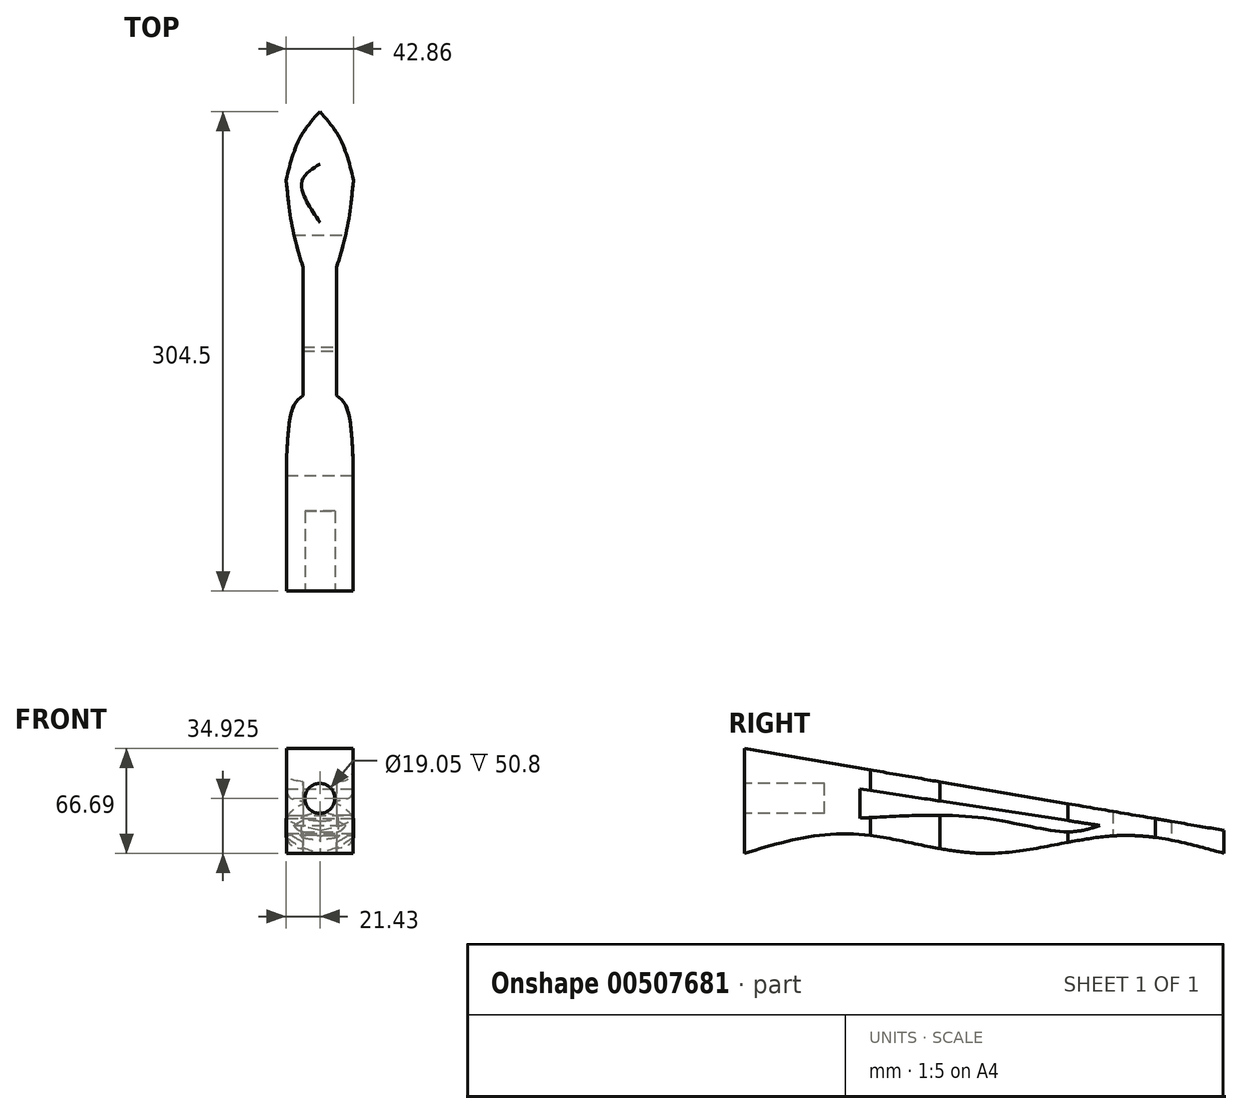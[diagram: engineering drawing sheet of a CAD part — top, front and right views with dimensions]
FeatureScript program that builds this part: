
annotation { "Feature Type Name" : "Feature", "Feature Type Description" : "" }
export const myFeature = defineFeature(function(context is Context, id is Id, definition is map)
    precondition{}
    {
        {
            var Q0;
            Q0=qCreatedBy(makeId("Right.planeOp"),FACE);
            var sketch = newSketch(context, id + "F0", { "sketchPlane" : qUnion([Q0])});
            skLineSegment(sketch, "E0", {"start": v(-152.4, 0) * mm, "end": v(152.4, 0) * mm});
            skLineSegment(sketch, "E1", {"start": v(-152.4, 0) * mm, "end": v(-152.4, 69.85) * mm});
            skLineSegment(sketch, "E2", {"start": v(152.4, 0) * mm, "end": v(152.4, 19.05) * mm});
            skLineSegment(sketch, "E3", {"start": v(152.4, 19.05) * mm, "end": v(-152.4, 69.85) * mm});
            skPoint(sketch, "E4.endSnap0", {"position": v(-152.4, 34.93) * mm});
            skLineSegment(sketch, "E5.0", {"start": v(-95.25, 50.8) * mm, "end": v(-152.4, 50.8) * mm, "construction": true});
            skLineSegment(sketch, "E5.1", {"start": v(-95.25, 50.8) * mm, "end": v(-95.25, 19.05) * mm, "construction": true});
            skLineSegment(sketch, "E5.2", {"start": v(-95.25, 19.05) * mm, "end": v(-152.4, 19.05) * mm, "construction": true});
            skSolve(sketch);
        }
        {
            var Q0;
            Q0=makeQuery(id+"F0.imprint","IMPRINT",FACE,{"disambiguationData":[TD([[makeQuery(id+"F0.imprint","IMPRINT",EDGE,{"derivedFrom":sQuery(id+"F0.wireOp",EDGE,"E0")}),1.0]])]});
            extrude(context, id + "F1", {"entities" : qUnion([Q0]), "depth" : 42.86 * mm, "symmetric" : true});
        }
        {
            var Q0;
            Q0=makeQuery(id+"F1.opExtrude","SWEPT_FACE",FACE,{"disambiguationData":[OSD([sQuery(id+"F0.wireOp",EDGE,"E1")])]});
            var sketch = newSketch(context, id + "F2", { "sketchPlane" : qUnion([Q0])});
            skLineSegment(sketch, "E6", {"start": v(21.43, 34.93) * mm, "end": v(0, 34.93) * mm, "construction": true});
            skCircle(sketch, "E7", {"center": v(0, 34.93) * mm, "radius": 9.53 * mm});
            skSolve(sketch);
        }
        {
            var Q0;
            Q0=makeQuery(id+"F2.imprint","IMPRINT",FACE,{"disambiguationData":[TD([[makeQuery(id+"F2.imprint","IMPRINT",EDGE,{"derivedFrom":sQuery(id+"F2.wireOp",EDGE,"E7")}),1.0]])]});
            var Q1;
            Q1=sQuery(id+"F2.wireOp",EDGE,"E7");
            extrude(context, id + "F3", {"entities" : qUnion([Q0]), "operationType" : NewBodyOperationType.REMOVE, "surfaceEntities" : qUnion([Q1]), "oppositeDirection" : true, "depth" : 50.8 * mm});
        }
        {
            var Q0;
            Q0=makeQuery(id+"F1.opExtrude","CAP_FACE",FACE,{"disambiguationData":[OSD([sQuery(id+"F0.wireOp",EDGE,"E0"),sQuery(id+"F0.wireOp",EDGE,"E1"),sQuery(id+"F0.wireOp",EDGE,"E2"),sQuery(id+"F0.wireOp",EDGE,"E3")])],"isStart":false});
            var sketch = newSketch(context, id + "F4", { "sketchPlane" : qUnion([Q0])});
            skLineSegment(sketch, "E8", {"start": v(-152.4, 34.93) * mm, "end": v(-152.4, 44.45) * mm, "construction": true});
            skLineSegment(sketch, "E9.0", {"start": v(-95.25, 19.05) * mm, "end": v(-152.4, 19.05) * mm, "construction": true});
            skLineSegment(sketch, "E9.1", {"start": v(-95.25, 50.8) * mm, "end": v(-95.25, 19.05) * mm, "construction": true});
            skLineSegment(sketch, "E9.2", {"start": v(-152.4, 50.8) * mm, "end": v(-95.25, 50.8) * mm, "construction": true});
            skLineSegment(sketch, "E10", {"start": v(57.15, 0) * mm, "end": v(57.15, 34.93) * mm, "construction": true});
            skLineSegment(sketch, "E11", {"start": v(-152.4, 44.45) * mm, "end": v(-101.6, 44.45) * mm, "construction": true});
            skLineSegment(sketch, "E12", {"start": v(-101.6, 44.45) * mm, "end": v(-101.6, 25.4) * mm, "construction": true});
            skLineSegment(sketch, "E13", {"start": v(-101.6, 25.4) * mm, "end": v(-152.4, 25.4) * mm, "construction": true});
            skSolve(sketch);
        }
        {
            var Q0;
            Q0=makeQuery(id+"F1.opExtrude","SWEPT_FACE",FACE,{"disambiguationData":[OSD([sQuery(id+"F0.wireOp",EDGE,"E0")])]});
            var sketch = newSketch(context, id + "F5", { "sketchPlane" : qUnion([Q0])});
            skLineSegment(sketch, "E14", {"start": v(0, 152.4) * mm, "end": v(0, -152.4) * mm, "construction": true});
            skLineSegment(sketch, "E15", {"start": v(21.43, -57.15) * mm, "end": v(-21.43, -57.15) * mm, "construction": true});
            skLineSegment(sketch, "E16", {"start": v(15.88, 152.4) * mm, "end": v(15.88, 95.25) * mm, "construction": true});
            skLineSegment(sketch, "E17", {"start": v(15.88, 95.25) * mm, "end": v(-15.87, 95.25) * mm, "construction": true});
            skLineSegment(sketch, "E18", {"start": v(-15.87, 95.25) * mm, "end": v(-15.87, 152.4) * mm, "construction": true});
            skLineSegment(sketch, "E19", {"start": v(0, 152.4) * mm, "end": v(-9.53, 152.4) * mm, "construction": true});
            skLineSegment(sketch, "E20", {"start": v(-9.53, 152.4) * mm, "end": v(-9.53, 101.6) * mm, "construction": true});
            skLineSegment(sketch, "E21", {"start": v(-9.52, 101.6) * mm, "end": v(9.53, 101.6) * mm, "construction": true});
            skLineSegment(sketch, "E22", {"start": v(9.53, 101.6) * mm, "end": v(9.53, 152.4) * mm, "construction": true});
            skSolve(sketch);
        }
        {
            var Q0;
            Q0=makeQuery(id+"F4.imprint","IMPRINT",FACE,{"disambiguationData":[TD([[makeQuery(id+"F4.imprint","IMPRINT",EDGE,{"derivedFrom":makeQuery(id+"F1.opExtrude","CAP_EDGE",EDGE,{"disambiguationData":[OSD([sQuery(id+"F0.wireOp",EDGE,"E0")])],"isStart":false})}),1.0]])]});
            var sketch = newSketch(context, id + "F6", { "sketchPlane" : qUnion([Q0])});
            skFitSpline(sketch, "E23", {"points": [v(-152.45, 0) * mm, v(-83.19, 12.39) * mm, v(0, 0) * mm, v(84.2, 11.28) * mm, v(152.36, 0) * mm], "startDerivative": vector(283.15, 85.12) * mm, "endDerivative": vector(279.7, -78.66) * mm});
            skLineSegment(sketch, "E24", {"start": v(152.36, 0) * mm, "end": v(152.36, 14.6) * mm});
            skLineSegment(sketch, "E25", {"start": v(152.36, 14.6) * mm, "end": v(-152.9, 66.78) * mm});
            skLineSegment(sketch, "E26", {"start": v(-152.9, 66.78) * mm, "end": v(-152.45, 0) * mm});
            skLineSegment(sketch, "E27", {"start": v(-78.97, 41.03) * mm, "end": v(-78.97, 22.38) * mm});
            skFitSpline(sketch, "E28", {"points": [v(-78.97, 22.38) * mm, v(0, 22.38) * mm, v(52.02, 13.72) * mm, v(73.55, 17.72) * mm], "startDerivative": vector(190.9, 11.16) * mm, "endDerivative": vector(86.31, 27.92) * mm});
            skLineSegment(sketch, "E29", {"start": v(-78.97, 41.03) * mm, "end": v(73.55, 17.72) * mm});
            skSolve(sketch);
        }
        {
            var Q0;
            Q0 = qSketchRegion(id + "F6", true);
            extrude(context, id + "F7", {"entities" : qUnion([Q0]), "operationType" : NewBodyOperationType.INTERSECT, "endBound" : BoundingType.THROUGH_ALL, "oppositeDirection" : true, "depth" : 25.4 * mm});
        }
        {
            var Q0;
            Q0=qCreatedBy(makeId("Top.planeOp"),FACE);
            var sketch = newSketch(context, id + "F8", { "sketchPlane" : qUnion([Q0])});
            skLineSegment(sketch, "E30", {"start": v(21.25, -152.7) * mm, "end": v(21.25, -72.27) * mm});
            skFitSpline(sketch, "E31", {"points": [v(21.25, -72.27) * mm, v(16.78, -35.22) * mm, v(10.67, -28.28) * mm], "startDerivative": vector(-2.79, 67.04) * mm, "endDerivative": vector(-20.34, 15.12) * mm});
            skLineSegment(sketch, "E32", {"start": v(10.67, -28.28) * mm, "end": v(10.67, 53.23) * mm});
            skFitSpline(sketch, "E33", {"points": [v(10.67, 53.23) * mm, v(17.03, 76.4) * mm, v(21.44, 108.64) * mm], "startDerivative": vector(15.07, 47.86) * mm, "endDerivative": vector(6.69, 62.6) * mm});
            skLineSegment(sketch, "E34.MirrorCS", {"start": v(-10.67, -28.28) * mm, "end": v(-10.67, 53.23) * mm});
            skFitSpline(sketch, "E35.MirrorCS", {"points": [v(-21.25, -72.27) * mm, v(-16.78, -35.22) * mm, v(-10.67, -28.28) * mm], "startDerivative": vector(2.79, 67.04) * mm, "endDerivative": vector(20.34, 15.12) * mm});
            skFitSpline(sketch, "E36.MirrorCS", {"points": [v(-10.67, 53.23) * mm, v(-17.03, 76.4) * mm, v(-21.44, 108.64) * mm], "startDerivative": vector(-15.07, 47.86) * mm, "endDerivative": vector(-6.69, 62.6) * mm});
            skLineSegment(sketch, "E37.MirrorCS", {"start": v(-21.25, -152.7) * mm, "end": v(-21.25, -72.27) * mm});
            skLineSegment(sketch, "E38", {"start": v(-21.25, -152.7) * mm, "end": v(21.25, -152.7) * mm});
            skFitSpline(sketch, "E39", {"points": [v(-21.44, 108.64) * mm, v(-12.87, 134.83) * mm, v(0, 152.1) * mm], "startDerivative": vector(13.16, 52.68) * mm, "endDerivative": vector(30.07, 33.86) * mm});
            skFitSpline(sketch, "E40.MirrorCS", {"points": [v(21.44, 108.64) * mm, v(12.87, 134.83) * mm, v(0, 152.1) * mm], "startDerivative": vector(-13.16, 52.68) * mm, "endDerivative": vector(-30.07, 33.86) * mm});
            skFitSpline(sketch, "E41", {"points": [v(0, 81.74) * mm, v(11.51, 107.29) * mm, v(0, 118.74) * mm], "startDerivative": vector(33.6, 50.25) * mm, "endDerivative": vector(-36.77, 22.5) * mm});
            skFitSpline(sketch, "E42.MirrorCS", {"points": [v(0, 81.74) * mm, v(-11.51, 107.29) * mm, v(0, 118.74) * mm], "startDerivative": vector(-33.6, 50.25) * mm, "endDerivative": vector(36.77, 22.5) * mm});
            skPoint(sketch, "E43.MirrorCS.end.orphan", {"position": v(0, -46.59) * mm});
            skPoint(sketch, "E43.MirrorCS.start.orphan", {"position": v(0, -86.1) * mm});
            skSolve(sketch);
        }
        {
            var Q0;
            Q0 = qSketchRegion(id + "F8", true);
            extrude(context, id + "F9", {"entities" : qUnion([Q0]), "operationType" : NewBodyOperationType.INTERSECT, "endBound" : BoundingType.THROUGH_ALL, "depth" : 25.4 * mm});
        }
    });
